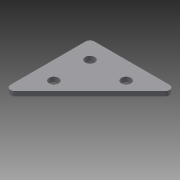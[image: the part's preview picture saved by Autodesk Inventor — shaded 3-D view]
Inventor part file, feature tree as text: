
AUTODESK INVENTOR PART (.ipt)
format: ipt  version: 2013 (Build 170138000, 138)  size: 87,552 bytes
history: native  units: in
note: dims shown in document units (in); Inventor stores cm internally (conversion verified against a paired STEP export)
features: extrude x1, sketch x1
ambient origin geometry x8: Origin, YZ Plane, XZ Plane, XY Plane, X Axis, Y Axis, Z Axis, Center Point
bodies: Solid1 (feature_tree)
feature tree (2):
  extrude  "Extrusion1"  Depth=0.266in
  sketch  "Sketch1"  dims[d3=0.266in d4=0.266in d5=0.266in d6=0.5in d7=0.5in d8=0.5in d9=1.0in d10=1.0in d11=0.5in d12=2.5in d13=2.5in d14=0.125in d15=0.125in d16=0.0in]
